# Revit family: Hager-Orion_Plus-IP65-D300-Cl.II-Poly_double_encl-630A-CH-de
name_source: partatom
category: Electrical Equipment
units: mm (PartAtom-declared; Revit-internal decimal feet)

## family parameters
Cut with Voids When Loaded = No
Host = Face
Panel Configuration = Two Columns, Circuits Across
Part Type = Panelboard
Room Calculation Point = No
Round Connector Dimension = Use Diameter
Shared = No

## types (6) — shared parameters
EF000003 - Montageart = EV000384 - Aufputz
EF000007 - Farbe = EV000270 - grau
EF000049 - Tiefe = 300 mm  [stored 0.984252 ft]
EF000116 - RAL-Nummer = 7035
EF000266 - Anzahl der Reihen = 3
EF001131 - Innentiefe = 300 mm  [stored 0.984252 ft]
EF001596 - Werkstoff des Gehäuses = EV000139 - Kunststoff
EF001613 - Funktionserhalt = EV000494 - ohne
EF004464 - Art der Tür = EV002646 - Einzel
EF005474 - Schutzart (IP) = EV006421 - IP65
EF006306 - Mit Schloss = Yes
EF007800 - Geeignet für Blitzschutz = No
EF008873 - Nennstrom (In) = 630 A
EF009170 - Materialstärke Gehäuse = 2 mm  [stored 0.00656168 ft]
EF009171 - Materialstärke Tür/Deckel = 2 mm  [stored 0.00656168 ft]
EF015940 - Deckel mit Überdruckentlastung = No
HG000003 - Bereich = Orion Plus
HG000006 - Unterputz = No
HG000010 - Asymmetrische Türen = No
HG000023 - Gehäuse mit doppeltem Querschnitt = Yes
HG000024 - Höhe des unteren Teils = 800 mm  [stored 2.62467 ft]
HG000026 - Stehend auf dem Boden = No
HG000027 - Sockelhöhe = 70 mm  [stored 0.229659 ft]
Manufacturer = Hager
Type Comments = Orion Plus
zero-valued in all types: Default Elevation, EF000218 - Einbautiefe, EF000437 - Anzahl der Leitungseinführungen, EF002950 - Breite in Teilungseinheiten, EF009554 - Anzahl der Öffnungen für Flanschplatten

## per-type parameters (varying)
| type | EF000008 - Breite | EF000040 - Höhe | EF000118 - Mit Montageplatte | EF000339 - Art der Abdeckung | EF001088 - Anbaumöglichkeit | EF003532 - Geeignet für Außengebrauch | EF004293 - Schlagfestigkeit | EF004427 - Anzahl der Module | EF006244 - Transparenter Deckel/Tür | EF009212 - Ausführung Deckel | HG000002 - Mit tür | HG000004 - Herstellerreferenz | HG000009 - Doppelflügeligen Tür |
| Aufputz IP65 B1100 H1150 T300  - FL360B | 1100 mm | 1150 mm | No | EV004216 - Tür | Yes | Yes | EV008784 - IK10 | 138 | Yes | EV009916 - mit Ausschnitt | Yes | FL360B | Yes |
| Aufputz IP65 B1100 H1450 T300  - FL362B | 1100 mm | 1450 mm | No | EV004216 - Tür | Yes | Yes | EV008784 - IK10 | 138 | Yes | EV009916 - mit Ausschnitt | Yes | FL362B | Yes |
| Aufputz IP65 B600 H1150 T300  - FL340B | 600 mm | 1150 mm | No | EV004216 - Tür | Yes | Yes | EV008784 - IK10 | 69 | Yes | EV009916 - mit Ausschnitt | Yes | FL340B | No |
| Aufputz IP65 B600 H1450 T300  - FL342B | 600 mm | 1450 mm | No | EV004216 - Tür | Yes | Yes | EV008784 - IK10 | 69 | Yes | EV009916 - mit Ausschnitt | No | FL342B | No |
| Aufputz IP65 B850 H1150 T300  - FL350B | 850 mm  [stored 2.78871 ft] | 1150 mm | No | EV004216 - Tür | Yes | Yes | EV008784 - IK10 | 111 | Yes | EV009916 - mit Ausschnitt | Yes | FL350B | No |
| Aufputz IP65 B850 H1450 T300  - FL352B | 850 mm  [stored 2.78871 ft] | 1450 mm | Yes | EV001012 - Deckel | No | No | EV006814 - IK08 | 111 | No | EV000116 - geschlossen | Yes | FL352B | No |

note: [stored X ft] marks values corroborated as IEEE doubles in the binary element streams (Revit-internal decimal feet)

## geometry (parser evidence)
native form markers: Sweep x10
no freeform markers — native parametric forms only
